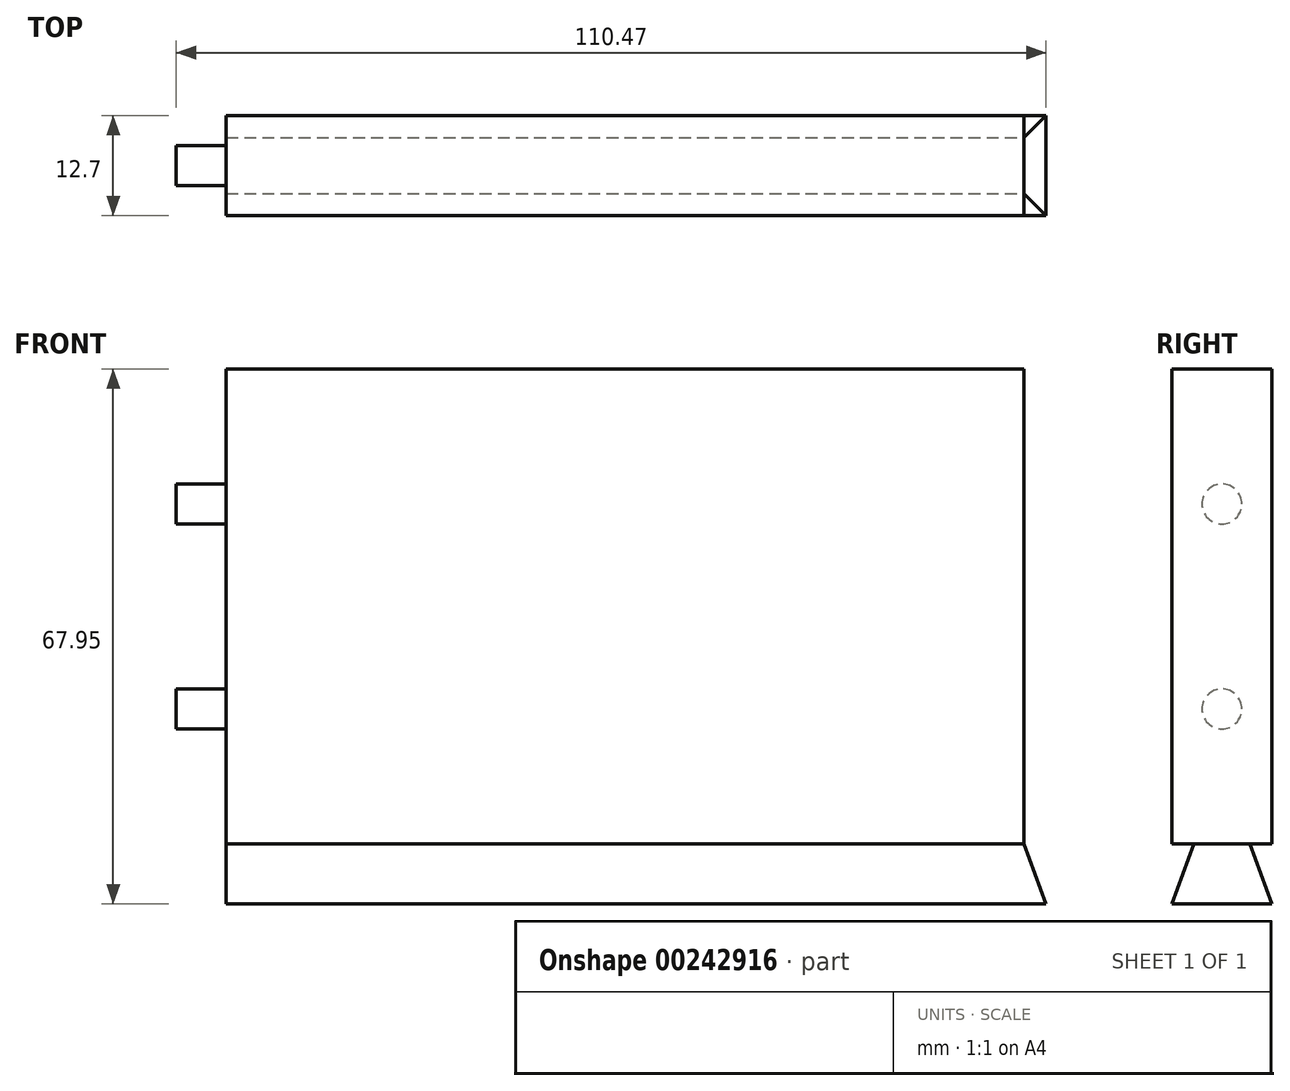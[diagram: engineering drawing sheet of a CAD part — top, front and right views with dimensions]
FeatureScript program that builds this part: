
annotation { "Feature Type Name" : "Feature", "Feature Type Description" : "" }
export const myFeature = defineFeature(function(context is Context, id is Id, definition is map)
    precondition{}
    {
        {
            var Q0;
            Q0=qCreatedBy(makeId("Front.planeOp"),FACE);
            var sketch = newSketch(context, id + "F0", { "sketchPlane" : qUnion([Q0])});
            skLineSegment(sketch, "E0", {"start": v(0, 0) * mm, "end": v(0, 60.33) * mm});
            skLineSegment(sketch, "E1", {"start": v(0, 60.33) * mm, "end": v(101.6, 60.33) * mm});
            skLineSegment(sketch, "E2", {"start": v(101.6, 60.33) * mm, "end": v(101.6, 0) * mm});
            skLineSegment(sketch, "E3", {"start": v(101.6, 0) * mm, "end": v(0, 0) * mm});
            skSolve(sketch);
        }
        {
            var Q0;
            Q0=makeQuery(id+"F0.imprint","IMPRINT",FACE,{"disambiguationData":[TD([[makeQuery(id+"F0.imprint","IMPRINT",EDGE,{"derivedFrom":sQuery(id+"F0.wireOp",EDGE,"E0")}),-1.0]])]});
            extrude(context, id + "F1", {"entities" : qUnion([Q0]), "depth" : 12.7 * mm});
        }
        {
            var Q0;
            Q0=makeQuery(id+"F1.opExtrude","SWEPT_FACE",FACE,{"disambiguationData":[OSD([sQuery(id+"F0.wireOp",EDGE,"E2")])]});
            var sketch = newSketch(context, id + "F2", { "sketchPlane" : qUnion([Q0])});
            skLineSegment(sketch, "E4.bottom", {"start": v(0, 0) * mm, "end": v(-12.7, 0) * mm});
            skLineSegment(sketch, "E4.top", {"start": v(0, -7.62) * mm, "end": v(-12.7, -7.62) * mm});
            skLineSegment(sketch, "E4.left", {"start": v(0, 0) * mm, "end": v(0, -7.62) * mm});
            skLineSegment(sketch, "E4.right", {"start": v(-12.7, 0) * mm, "end": v(-12.7, -7.62) * mm});
            skLineSegment(sketch, "E5", {"start": v(-12.7, -7.62) * mm, "end": v(-9.93, 0) * mm});
            skLineSegment(sketch, "E6", {"start": v(-9.93, 0) * mm, "end": v(-2.77, 0) * mm});
            skLineSegment(sketch, "E7", {"start": v(-2.77, 0) * mm, "end": v(0, -7.62) * mm});
            skSolve(sketch);
        }
        {
            var Q0;
            Q0=makeQuery(id+"F2.imprint","IMPRINT",FACE,{"disambiguationData":[TD([[makeQuery(id+"F2.imprint","IMPRINT",EDGE,{"derivedFrom":sQuery(id+"F2.wireOp",EDGE,"E4.top")}),-1.0]])]});
            extrude(context, id + "F3", {"entities" : qUnion([Q0]), "operationType" : NewBodyOperationType.ADD, "oppositeDirection" : true, "depth" : 101.6 * mm});
        }
        {
            var Q0;
            Q0=makeQuery(id+"F3.boolean.opBoolean","MERGE",FACE,{"derivedFrom":[makeQuery(id+"F1.opExtrude","SWEPT_FACE",FACE,{"disambiguationData":[OSD([sQuery(id+"F0.wireOp",EDGE,"E0")])]}),makeQuery(id+"F3.opExtrude","CAP_FACE",FACE,{"disambiguationData":[OSD([sQuery(id+"F2.wireOp",EDGE,"E4.top"),sQuery(id+"F2.wireOp",EDGE,"E5"),sQuery(id+"F2.wireOp",EDGE,"E6"),sQuery(id+"F2.wireOp",EDGE,"E7")])],"isStart":false})]});
            var sketch = newSketch(context, id + "F4", { "sketchPlane" : qUnion([Q0])});
            skLineSegment(sketch, "E8.bottom", {"start": v(0, 0) * mm, "end": v(13.76, 0) * mm});
            skLineSegment(sketch, "E8.top", {"start": v(0, -10.2) * mm, "end": v(13.76, -10.2) * mm});
            skLineSegment(sketch, "E8.left", {"start": v(0, 0) * mm, "end": v(0, -10.2) * mm});
            skLineSegment(sketch, "E8.right", {"start": v(13.76, 0) * mm, "end": v(13.76, -10.2) * mm});
            skSolve(sketch);
        }
        {
            var Q0;
            Q0 = qSketchRegion(id + "F4", true);
            extrude(context, id + "F5", {"entities" : qUnion([Q0]), "operationType" : NewBodyOperationType.REMOVE, "oppositeDirection" : true, "depth" : 3.17 * mm});
        }
        {
            var Q0;
            Q0=makeQuery(id+"F5.boolean.opBoolean","COPY",FACE,{"derivedFrom":makeQuery(id+"F5.opExtrude","CAP_FACE",FACE,{"disambiguationData":[OSD([sQuery(id+"F4.wireOp",EDGE,"E8.bottom"),sQuery(id+"F4.wireOp",EDGE,"E8.top"),sQuery(id+"F4.wireOp",EDGE,"E8.left"),sQuery(id+"F4.wireOp",EDGE,"E8.right")])],"isStart":false})});
            extrude(context, id + "F6", {"entities" : qUnion([Q0]), "operationType" : NewBodyOperationType.ADD, "depth" : 3.17 * mm});
        }
        {
            var Q0;
            Q0=makeQuery(id+"F1.opExtrude","SWEPT_FACE",FACE,{"disambiguationData":[OSD([sQuery(id+"F0.wireOp",EDGE,"E1")])]});
            var sketch = newSketch(context, id + "F7", { "sketchPlane" : qUnion([Q0])});
            skLineSegment(sketch, "E9.bottom", {"start": v(101.6, -12.7) * mm, "end": v(101.35, -12.7) * mm});
            skLineSegment(sketch, "E9.top", {"start": v(101.6, 0) * mm, "end": v(101.35, 0) * mm});
            skLineSegment(sketch, "E9.left", {"start": v(101.6, -12.7) * mm, "end": v(101.6, 0) * mm});
            skLineSegment(sketch, "E9.right", {"start": v(101.35, -12.7) * mm, "end": v(101.35, 0) * mm});
            skSolve(sketch);
        }
        {
            var Q0;
            Q0=makeQuery(id+"F7.imprint","IMPRINT",FACE,{"disambiguationData":[TD([[makeQuery(id+"F7.imprint","IMPRINT",EDGE,{"derivedFrom":sQuery(id+"F7.wireOp",EDGE,"E9.bottom")}),1.0]])]});
            extrude(context, id + "F8", {"entities" : qUnion([Q0]), "operationType" : NewBodyOperationType.REMOVE, "oppositeDirection" : true, "depth" : 101.6 * mm});
        }
        {
            var Q0;
            Q0=makeQuery(id+"F8.boolean.opBoolean","COPY",FACE,{"derivedFrom":makeQuery(id+"F8.opExtrude","SWEPT_FACE",FACE,{"disambiguationData":[OSD([sQuery(id+"F7.wireOp",EDGE,"E9.right")])]})});
            var sketch = newSketch(context, id + "F9", { "sketchPlane" : qUnion([Q0])});
            skLineSegment(sketch, "E10", {"start": v(-12.7, -7.62) * mm, "end": v(-9.93, 0) * mm});
            skLineSegment(sketch, "E11", {"start": v(-9.93, 0) * mm, "end": v(-2.77, 0) * mm});
            skLineSegment(sketch, "E12", {"start": v(-2.77, 0) * mm, "end": v(0, -7.62) * mm});
            skLineSegment(sketch, "E13", {"start": v(0, -7.62) * mm, "end": v(-12.7, -7.62) * mm});
            skSolve(sketch);
        }
        {
            var Q0;
            Q0=makeQuery(id+"F9.imprint","IMPRINT",FACE,{"disambiguationData":[TD([[makeQuery(id+"F9.imprint","IMPRINT",EDGE,{"derivedFrom":sQuery(id+"F9.wireOp",EDGE,"E10")}),1.0]])]});
            extrude(context, id + "F10", {"entities" : qUnion([Q0]), "operationType" : NewBodyOperationType.REMOVE, "oppositeDirection" : true, "depth" : 25.4 * mm});
        }
        {
            var Q0;
            Q0=makeQuery(id+"F10.boolean.opBoolean","COPY",FACE,{"derivedFrom":makeQuery(id+"F10.opExtrude","CAP_FACE",FACE,{"disambiguationData":[OSD([sQuery(id+"F9.wireOp",EDGE,"E10"),sQuery(id+"F9.wireOp",EDGE,"E11"),sQuery(id+"F9.wireOp",EDGE,"E12"),sQuery(id+"F9.wireOp",EDGE,"E13")])],"isStart":false})});
            var sketch = newSketch(context, id + "F11", { "sketchPlane" : qUnion([Q0])});
            skLineSegment(sketch, "E14", {"start": v(-12.7, -7.62) * mm, "end": v(-9.93, 0) * mm});
            skLineSegment(sketch, "E15", {"start": v(-9.93, 0) * mm, "end": v(-9.93, -7.62) * mm});
            skLineSegment(sketch, "E16", {"start": v(-9.93, -7.62) * mm, "end": v(-12.7, -7.62) * mm});
            skLineSegment(sketch, "E17", {"start": v(-9.93, 0) * mm, "end": v(-9.22, 0) * mm});
            skLineSegment(sketch, "E18", {"start": v(-9.22, 0) * mm, "end": v(-9.22, -7.62) * mm});
            skLineSegment(sketch, "E19", {"start": v(-9.22, -7.62) * mm, "end": v(-9.93, -7.62) * mm});
            skSolve(sketch);
        }
        {
            var Q0;
            {var subQ2=sQuery(id+"F2.wireOp",EDGE,"E7");var subQ4=sQuery(id+"F2.wireOp",EDGE,"E5");var subQ10=sQuery(id+"F4.wireOp",EDGE,"E8.bottom");var subQ12=sQuery(id+"F0.wireOp",EDGE,"E3");var subQ18=makeQuery(id+"F3.opExtrude","SWEPT_FACE",FACE,{"disambiguationData":[OSD([subQ4])]});var subQ19=makeQuery(id+"F1.opExtrude","SWEPT_FACE",FACE,{"disambiguationData":[OSD([subQ12])]});var subQ21=makeQuery(id+"F3.opExtrude","SWEPT_FACE",FACE,{"disambiguationData":[OSD([subQ2])]});var subQ22=makeQuery(id+"F5.boolean.opBoolean","MERGE",FACE,{"derivedFrom":[makeQuery(id+"F3.boolean.opBoolean","SPLIT",FACE,{"disambiguationData":[TD([subQ21])],"derivedFrom":subQ19}),makeQuery(id+"F3.boolean.opBoolean","SPLIT",FACE,{"disambiguationData":[TD([subQ18])],"derivedFrom":subQ19}),makeQuery(id+"F5.opExtrude","SWEPT_FACE",FACE,{"disambiguationData":[OSD([subQ10])]})]});Q0=makeQuery(id+"F10.boolean.opBoolean","MERGE",FACE,{"derivedFrom":[makeQuery(id+"F6.boolean.opBoolean","SPLIT",FACE,{"disambiguationData":[TD([subQ21])],"derivedFrom":subQ22}),makeQuery(id+"F6.boolean.opBoolean","SPLIT",FACE,{"disambiguationData":[TD([subQ18])],"derivedFrom":subQ22}),makeQuery(id+"F10.opExtrude","SWEPT_FACE",FACE,{"disambiguationData":[OSD([sQuery(id+"F9.wireOp",EDGE,"E11")])]})]});}
            var sketch = newSketch(context, id + "F12", { "sketchPlane" : qUnion([Q0])});
            skLineSegment(sketch, "E20", {"start": v(75.95, 9.93) * mm, "end": v(101.35, 9.93) * mm});
            skLineSegment(sketch, "E21", {"start": v(75.95, 2.77) * mm, "end": v(101.35, 2.77) * mm});
            skLineSegment(sketch, "E22", {"start": v(101.35, 2.77) * mm, "end": v(101.35, 9.93) * mm});
            skSolve(sketch);
        }
        {
            var Q0;
            Q0=makeQuery(id+"F11.imprint","IMPRINT",FACE,{"disambiguationData":[TD([[makeQuery(id+"F11.imprint","IMPRINT",EDGE,{"derivedFrom":sQuery(id+"F11.wireOp",EDGE,"E14")}),1.0]])]});
            var Q1;
            Q1=makeQuery(id+"F11.imprint","IMPRINT",FACE,{"disambiguationData":[TD([[makeQuery(id+"F11.imprint","IMPRINT",EDGE,{"derivedFrom":sQuery(id+"F11.wireOp",EDGE,"E15")}),1.0]])]});
            var Q2;
            Q2=sQuery(id+"F12.wireOp",EDGE,"E20");
            var Q3;
            Q3=sQuery(id+"F12.wireOp",EDGE,"E22");
            var Q4;
            Q4=sQuery(id+"F12.wireOp",EDGE,"E21");
            sweep(context, id + "F13", {"operationType" : NewBodyOperationType.ADD, "profiles" : qUnion([Q0, Q1]), "path" : qUnion([Q2, Q3, Q4])});
        }
        {
            var Q0;
            {var subQ0=sQuery(id+"F2.wireOp",EDGE,"E4.top");Q0=makeQuery(id+"F13.boolean.opBoolean","MERGE",FACE,{"derivedFrom":[makeQuery(id+"F6.boolean.opBoolean","MERGE",FACE,{"derivedFrom":[makeQuery(id+"F3.opExtrude","SWEPT_FACE",FACE,{"disambiguationData":[OSD([subQ0])]}),makeQuery(id+"F6.opExtrude","SWEPT_FACE",FACE,{"disambiguationData":[OSD([subQ0,sQuery(id+"F4.wireOp",EDGE,"E8.bottom"),sQuery(id+"F4.wireOp",EDGE,"E8.top"),sQuery(id+"F4.wireOp",EDGE,"E8.left"),sQuery(id+"F4.wireOp",EDGE,"E8.right")])]})]}),makeQuery(id+"F13.opSweep","SWEPT_FACE",FACE,{"disambiguationData":[OSD([sQuery(id+"F11.wireOp",EDGE,"E16"),sQuery(id+"F11.wireOp",EDGE,"E19"),sQuery(id+"F12.wireOp",EDGE,"E20")])]})]});}
            var sketch = newSketch(context, id + "F14", { "sketchPlane" : qUnion([Q0])});
            skLineSegment(sketch, "E23.bottom", {"start": v(75.95, 9.22) * mm, "end": v(100.64, 9.22) * mm});
            skLineSegment(sketch, "E23.top", {"start": v(75.95, 3.48) * mm, "end": v(100.64, 3.48) * mm});
            skLineSegment(sketch, "E23.left", {"start": v(75.95, 9.22) * mm, "end": v(75.95, 3.48) * mm});
            skLineSegment(sketch, "E23.right", {"start": v(100.64, 9.22) * mm, "end": v(100.64, 3.48) * mm});
            skSolve(sketch);
        }
        {
            var Q0;
            Q0=makeQuery(id+"F14.imprint","IMPRINT",FACE,{"disambiguationData":[TD([[makeQuery(id+"F14.imprint","IMPRINT",EDGE,{"derivedFrom":sQuery(id+"F14.wireOp",EDGE,"E23.bottom")}),-1.0]])]});
            extrude(context, id + "F15", {"entities" : qUnion([Q0]), "operationType" : NewBodyOperationType.ADD, "oppositeDirection" : true, "depth" : 7.62 * mm});
        }
        {
            var Q0;
            Q0=makeQuery(id+"F6.boolean.opBoolean","MERGE",FACE,{"derivedFrom":[makeQuery(id+"F3.boolean.opBoolean","MERGE",FACE,{"derivedFrom":[makeQuery(id+"F1.opExtrude","SWEPT_FACE",FACE,{"disambiguationData":[OSD([sQuery(id+"F0.wireOp",EDGE,"E0")])]}),makeQuery(id+"F3.opExtrude","CAP_FACE",FACE,{"disambiguationData":[OSD([sQuery(id+"F2.wireOp",EDGE,"E4.top"),sQuery(id+"F2.wireOp",EDGE,"E5"),sQuery(id+"F2.wireOp",EDGE,"E6"),sQuery(id+"F2.wireOp",EDGE,"E7")])],"isStart":false})]}),makeQuery(id+"F6.opExtrude","CAP_FACE",FACE,{"disambiguationData":[OSD([sQuery(id+"F4.wireOp",EDGE,"E8.bottom"),sQuery(id+"F4.wireOp",EDGE,"E8.top"),sQuery(id+"F4.wireOp",EDGE,"E8.left"),sQuery(id+"F4.wireOp",EDGE,"E8.right")])],"isStart":false})]});
            var sketch = newSketch(context, id + "F16", { "sketchPlane" : qUnion([Q0])});
            skLineSegment(sketch, "E24", {"start": v(0, 0) * mm, "end": v(0, 43.18) * mm});
            skLineSegment(sketch, "E25", {"start": v(0, 43.18) * mm, "end": v(12.7, 43.18) * mm});
            skCircle(sketch, "E26", {"center": v(6.35, 43.18) * mm, "radius": 2.54 * mm});
            skLineSegment(sketch, "E27", {"start": v(12.7, 0) * mm, "end": v(12.7, 17.15) * mm});
            skLineSegment(sketch, "E28", {"start": v(12.7, 17.15) * mm, "end": v(0, 17.15) * mm});
            skCircle(sketch, "E29", {"center": v(6.35, 17.15) * mm, "radius": 2.54 * mm});
            skSolve(sketch);
        }
        {
            var Q0;
            {var subQ0=sQuery(id+"F16.wireOp",EDGE,"E26");var subQ1=sQuery(id+"F16.wireOp",EDGE,"E25");var subQ2=makeQuery(id+"F16.imprint","INTERSECT",VERTEX,{"disambiguationData":[OD(0.0)],"derivedFrom":[subQ1,subQ0]});Q0=makeQuery(id+"F16.imprint","IMPRINT",FACE,{"disambiguationData":[TD([[makeQuery(id+"F16.imprint","IMPRINT",EDGE,{"disambiguationData":[TD([[subQ2,-1.0]])],"derivedFrom":subQ1}),1.0]])]});}
            var Q1;
            {var subQ0=sQuery(id+"F16.wireOp",EDGE,"E26");var subQ1=sQuery(id+"F16.wireOp",EDGE,"E25");var subQ2=makeQuery(id+"F16.imprint","INTERSECT",VERTEX,{"disambiguationData":[OD(0.0)],"derivedFrom":[subQ1,subQ0]});Q1=makeQuery(id+"F16.imprint","IMPRINT",FACE,{"disambiguationData":[TD([[makeQuery(id+"F16.imprint","IMPRINT",EDGE,{"disambiguationData":[TD([[subQ2,-1.0]])],"derivedFrom":subQ1}),-1.0]])]});}
            var Q2;
            {var subQ0=sQuery(id+"F16.wireOp",EDGE,"E29");var subQ1=sQuery(id+"F16.wireOp",EDGE,"E28");var subQ2=makeQuery(id+"F16.imprint","INTERSECT",VERTEX,{"disambiguationData":[OD(0.0)],"derivedFrom":[subQ1,subQ0]});Q2=makeQuery(id+"F16.imprint","IMPRINT",FACE,{"disambiguationData":[TD([[makeQuery(id+"F16.imprint","IMPRINT",EDGE,{"disambiguationData":[TD([[subQ2,-1.0]])],"derivedFrom":subQ1}),1.0]])]});}
            var Q3;
            {var subQ0=sQuery(id+"F16.wireOp",EDGE,"E29");var subQ1=sQuery(id+"F16.wireOp",EDGE,"E28");var subQ2=makeQuery(id+"F16.imprint","INTERSECT",VERTEX,{"disambiguationData":[OD(0.0)],"derivedFrom":[subQ1,subQ0]});Q3=makeQuery(id+"F16.imprint","IMPRINT",FACE,{"disambiguationData":[TD([[makeQuery(id+"F16.imprint","IMPRINT",EDGE,{"disambiguationData":[TD([[subQ2,-1.0]])],"derivedFrom":subQ1}),-1.0]])]});}
            extrude(context, id + "F17", {"entities" : qUnion([Q0, Q1, Q2, Q3]), "operationType" : NewBodyOperationType.ADD, "depth" : 6.35 * mm});
        }
    });
